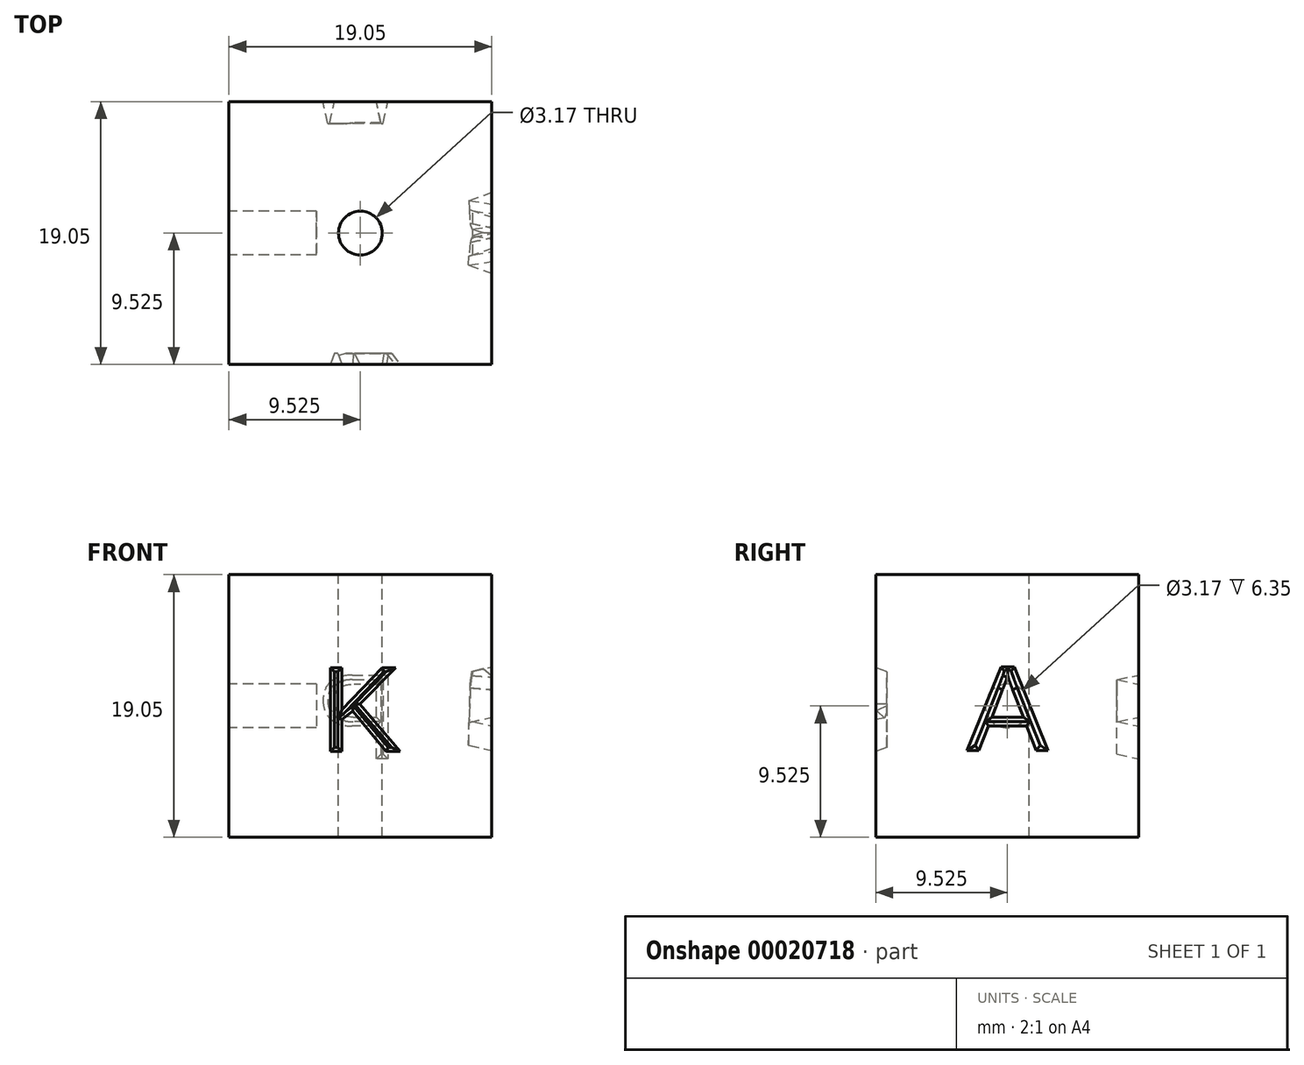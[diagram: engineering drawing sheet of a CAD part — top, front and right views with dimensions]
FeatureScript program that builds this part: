
annotation { "Feature Type Name" : "Feature", "Feature Type Description" : "" }
export const myFeature = defineFeature(function(context is Context, id is Id, definition is map)
    precondition{}
    {
        {
            var Q0;
            Q0=qCreatedBy(makeId("Top.planeOp"),FACE);
            var sketch = newSketch(context, id + "F0", { "sketchPlane" : qUnion([Q0])});
            skLineSegment(sketch, "E0.bottom", {"start": v(0, 0) * mm, "end": v(19.05, 0) * mm});
            skLineSegment(sketch, "E0.top", {"start": v(0, 19.05) * mm, "end": v(19.05, 19.05) * mm});
            skLineSegment(sketch, "E0.left", {"start": v(0, 0) * mm, "end": v(0, 19.05) * mm});
            skLineSegment(sketch, "E0.right", {"start": v(19.05, 0) * mm, "end": v(19.05, 19.05) * mm});
            skSolve(sketch);
        }
        {
            var Q0;
            Q0 = qSketchRegion(id + "F0", true);
            extrude(context, id + "F1", {"entities" : qUnion([Q0]), "depth" : 19.05 * mm});
        }
        {
            var Q0;
            Q0=makeQuery(id+"F1.opExtrude","SWEPT_FACE",FACE,{"disambiguationData":[OSD([sQuery(id+"F0.wireOp",EDGE,"E0.bottom")])]});
            var sketch = newSketch(context, id + "F2", { "sketchPlane" : qUnion([Q0])});
            skText(sketch, "E1", { "text": "K", "fontName": "Arimo-Regular.ttf"});
            skPoint(sketch, "E2", {"position": v(9.53, 19.05) * mm});
            const initialGuessF2  = {"E1": [0.00663, 0.00622, 1, 0, 0.00635]};
            skSetInitialGuess(sketch, initialGuessF2);
            skSolve(sketch);
        }
        {
            var Q0;
            Q0=makeQuery(id+"F2.imprint","IMPRINT",FACE,{"disambiguationData":[TD([[makeQuery(id+"F2.imprint","IMPRINT",EDGE,{"derivedFrom":sQuery(id+"F2.wireOp",EDGE,"E1.sketch_text.stroke-0")}),-1.0]])]});
            extrude(context, id + "F3", {"entities" : qUnion([Q0]), "operationType" : NewBodyOperationType.REMOVE, "oppositeDirection" : true, "depth" : 0.8 * mm, "hasDraft" : true, "draftAngle" : 20 * degree, "draftPullDirection" : true});
        }
        {
            var Q0;
            Q0=makeQuery(id+"F1.opExtrude","SWEPT_FACE",FACE,{"disambiguationData":[OSD([sQuery(id+"F0.wireOp",EDGE,"E0.right")])]});
            var sketch = newSketch(context, id + "F4", { "sketchPlane" : qUnion([Q0])});
            skText(sketch, "E3", { "text": "A", "fontName": "Arimo-Regular.ttf"});
            skPoint(sketch, "E4", {"position": v(9.53, 19.05) * mm});
            const initialGuessF4  = {"E3": [0.0066, 0.0063, 1, 0, 0.00635]};
            skSetInitialGuess(sketch, initialGuessF4);
            skSolve(sketch);
        }
        {
            var Q0;
            Q0 = qSketchRegion(id + "F4", true);
            extrude(context, id + "F5", {"entities" : qUnion([Q0]), "operationType" : NewBodyOperationType.REMOVE, "oppositeDirection" : true, "depth" : 1.71 * mm, "hasDraft" : true, "draftAngle" : 13 * degree, "draftPullDirection" : true});
        }
        {
            var Q0;
            Q0=makeQuery(id+"F1.opExtrude","SWEPT_FACE",FACE,{"disambiguationData":[OSD([sQuery(id+"F0.wireOp",EDGE,"E0.left")])]});
            var sketch = newSketch(context, id + "F6", { "sketchPlane" : qUnion([Q0])});
            skCircle(sketch, "E5", {"center": v(-9.52, 9.53) * mm, "radius": 1.59 * mm});
            skSolve(sketch);
        }
        {
            var Q0;
            Q0 = qSketchRegion(id + "F6", true);
            extrude(context, id + "F7", {"entities" : qUnion([Q0]), "operationType" : NewBodyOperationType.REMOVE, "oppositeDirection" : true, "depth" : 6.35 * mm});
        }
        {
            var Q0;
            Q0=makeQuery(id+"F1.opExtrude","SWEPT_FACE",FACE,{"disambiguationData":[OSD([sQuery(id+"F0.wireOp",EDGE,"E0.top")])]});
            var sketch = newSketch(context, id + "F8", { "sketchPlane" : qUnion([Q0])});
            skText(sketch, "E6", { "text": "P", "fontName": "Arimo-Regular.ttf"});
            skPoint(sketch, "E7", {"position": v(-9.53, 19.05) * mm});
            const initialGuessF8  = {"E6": [-0.01223, 0.0057, 1, 0, 0.00635]};
            skSetInitialGuess(sketch, initialGuessF8);
            skSolve(sketch);
        }
        {
            var Q0;
            Q0=makeQuery(id+"F8.imprint","IMPRINT",FACE,{"disambiguationData":[TD([[makeQuery(id+"F8.imprint","IMPRINT",EDGE,{"derivedFrom":sQuery(id+"F8.wireOp",EDGE,"E6.sketch_text.stroke-0")}),-1.0]])]});
            extrude(context, id + "F9", {"entities" : qUnion([Q0]), "operationType" : NewBodyOperationType.REMOVE, "oppositeDirection" : true, "depth" : 1.59 * mm, "hasDraft" : true, "draftAngle" : 12 * degree, "draftPullDirection" : true});
        }
        {
            var Q0;
            Q0=makeQuery(id+"F1.opExtrude","CAP_FACE",FACE,{"disambiguationData":[OSD([sQuery(id+"F0.wireOp",EDGE,"E0.bottom"),sQuery(id+"F0.wireOp",EDGE,"E0.top"),sQuery(id+"F0.wireOp",EDGE,"E0.left"),sQuery(id+"F0.wireOp",EDGE,"E0.right")])],"isStart":false});
            var sketch = newSketch(context, id + "F10", { "sketchPlane" : qUnion([Q0])});
            skCircle(sketch, "E8", {"center": v(9.53, 9.53) * mm, "radius": 1.59 * mm});
            skSolve(sketch);
        }
        {
            var Q0;
            Q0 = qSketchRegion(id + "F10", true);
            extrude(context, id + "F11", {"entities" : qUnion([Q0]), "operationType" : NewBodyOperationType.REMOVE, "endBound" : BoundingType.THROUGH_ALL, "oppositeDirection" : true, "depth" : 25.4 * mm});
        }
    });
